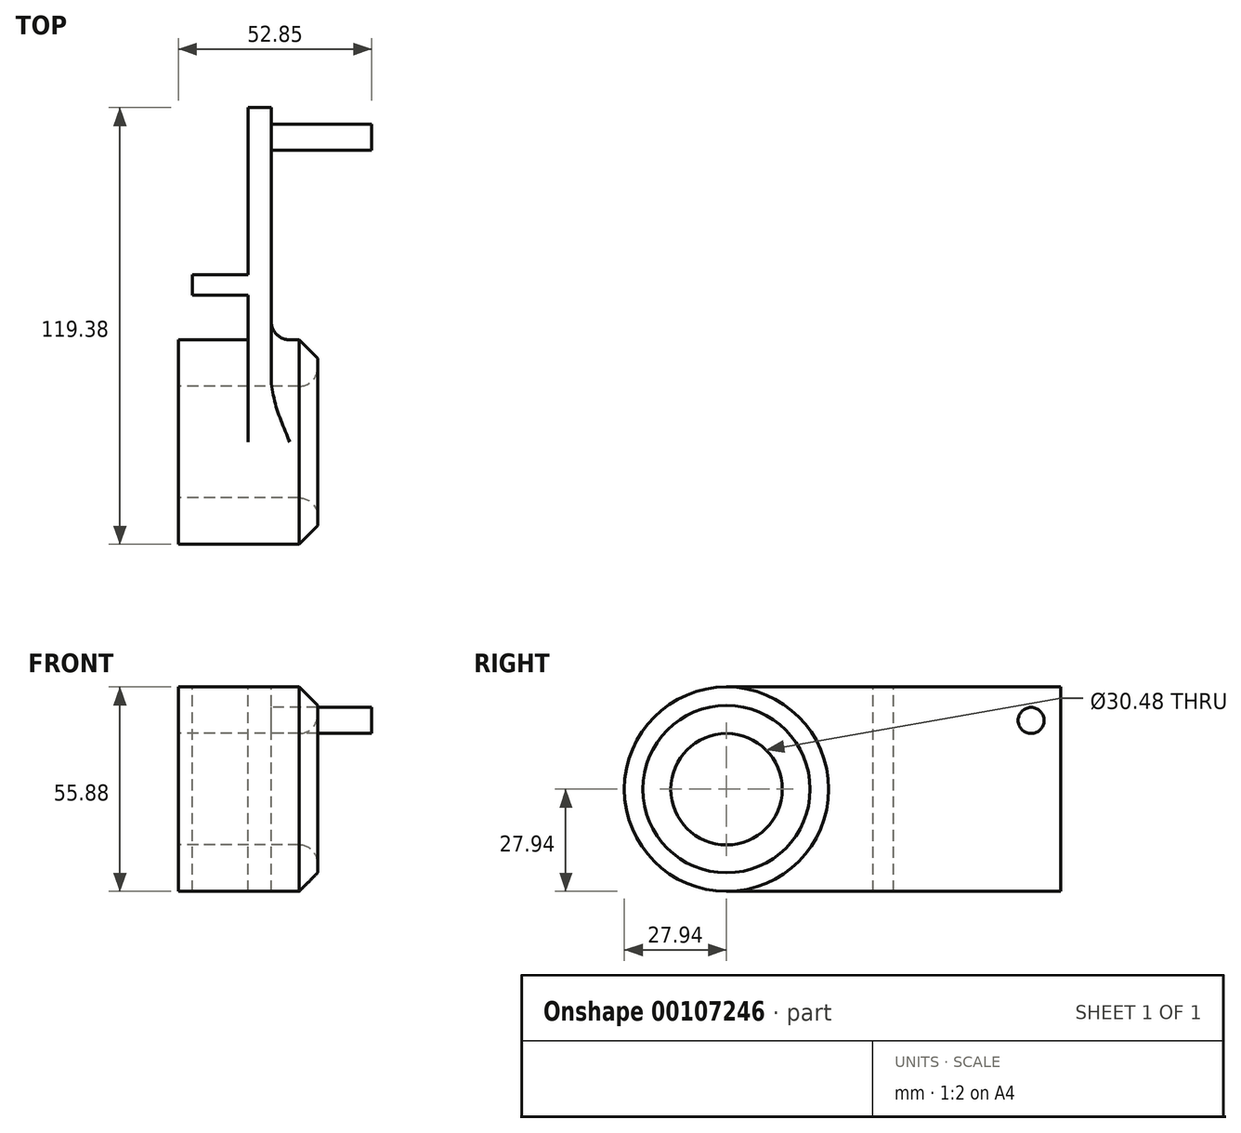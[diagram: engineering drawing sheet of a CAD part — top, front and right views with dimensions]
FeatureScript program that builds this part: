
annotation { "Feature Type Name" : "Feature", "Feature Type Description" : "" }
export const myFeature = defineFeature(function(context is Context, id is Id, definition is map)
    precondition{}
    {
        {
            var Q0;
            Q0=qCreatedBy(makeId("Right.planeOp"),FACE);
            var sketch = newSketch(context, id + "F0", { "sketchPlane" : qUnion([Q0])});
            skLineSegment(sketch, "E0.bottom", {"start": v(45.72, -27.94) * mm, "end": v(-45.72, -27.94) * mm});
            skLineSegment(sketch, "E0.top", {"start": v(45.72, 27.94) * mm, "end": v(-45.72, 27.94) * mm});
            skLineSegment(sketch, "E0.left", {"start": v(45.72, -27.94) * mm, "end": v(45.72, 27.94) * mm});
            skLineSegment(sketch, "E0.right", {"start": v(-45.72, -27.94) * mm, "end": v(-45.72, 27.94) * mm});
            skPoint(sketch, "E0.middle", {"position": v(0, 0) * mm});
            skCircle(sketch, "E1", {"center": v(-45.72, 0) * mm, "radius": 27.94 * mm});
            skCircle(sketch, "E2", {"center": v(-45.72, 0) * mm, "radius": 15.24 * mm});
            skSolve(sketch);
        }
        {
            var Q0;
            {var subQ0=sQuery(id+"F0.wireOp",EDGE,"E0.bottom");Q0=makeQuery(id+"F0.imprint","IMPRINT",FACE,{"disambiguationData":[TD([[makeQuery(id+"F0.imprint","IMPRINT",EDGE,{"derivedFrom":subQ0}),-1.0]])]});}
            var Q1;
            {var subQ1=sQuery(id+"F0.wireOp",EDGE,"E0.right");var subQ3=sQuery(id+"F0.wireOp",EDGE,"E2");var subQ4=makeQuery(id+"F0.imprint","INTERSECT",VERTEX,{"disambiguationData":[OD(0.0)],"derivedFrom":[subQ1,subQ3]});Q1=makeQuery(id+"F0.imprint","IMPRINT",FACE,{"disambiguationData":[TD([[makeQuery(id+"F0.imprint","IMPRINT",EDGE,{"disambiguationData":[TD([[subQ4,-1.0]])],"derivedFrom":subQ3}),-1.0]])]});}
            var Q2;
            {var subQ1=sQuery(id+"F0.wireOp",EDGE,"E0.right");var subQ3=sQuery(id+"F0.wireOp",EDGE,"E2");var subQ4=makeQuery(id+"F0.imprint","INTERSECT",VERTEX,{"disambiguationData":[OD(0.0)],"derivedFrom":[subQ1,subQ3]});Q2=makeQuery(id+"F0.imprint","IMPRINT",FACE,{"disambiguationData":[TD([[makeQuery(id+"F0.imprint","IMPRINT",EDGE,{"disambiguationData":[TD([[subQ4,1.0]])],"derivedFrom":subQ3}),-1.0]])]});}
            var Q3;
            {var subQ0=sQuery(id+"F0.wireOp",EDGE,"E2");var subQ1=sQuery(id+"F0.wireOp",EDGE,"E0.right");var subQ2=makeQuery(id+"F0.imprint","INTERSECT",VERTEX,{"disambiguationData":[OD(0.0)],"derivedFrom":[subQ1,subQ0]});Q3=makeQuery(id+"F0.imprint","IMPRINT",FACE,{"disambiguationData":[TD([[makeQuery(id+"F0.imprint","IMPRINT",EDGE,{"disambiguationData":[TD([[subQ2,-1.0]])],"derivedFrom":subQ1}),1.0]])]});}
            var Q4;
            {var subQ0=sQuery(id+"F0.wireOp",EDGE,"E2");var subQ1=sQuery(id+"F0.wireOp",EDGE,"E0.right");var subQ2=makeQuery(id+"F0.imprint","INTERSECT",VERTEX,{"disambiguationData":[OD(0.0)],"derivedFrom":[subQ1,subQ0]});Q4=makeQuery(id+"F0.imprint","IMPRINT",FACE,{"disambiguationData":[TD([[makeQuery(id+"F0.imprint","IMPRINT",EDGE,{"disambiguationData":[TD([[subQ2,-1.0]])],"derivedFrom":subQ1}),-1.0]])]});}
            extrude(context, id + "F1", {"entities" : qUnion([Q0, Q1, Q2, Q3, Q4]), "depth" : 6.35 * mm});
        }
        {
            var Q0;
            {var subQ1=sQuery(id+"F0.wireOp",EDGE,"E0.right");var subQ3=sQuery(id+"F0.wireOp",EDGE,"E2");var subQ4=makeQuery(id+"F0.imprint","INTERSECT",VERTEX,{"disambiguationData":[OD(0.0)],"derivedFrom":[subQ1,subQ3]});Q0=makeQuery(id+"F0.imprint","IMPRINT",FACE,{"disambiguationData":[TD([[makeQuery(id+"F0.imprint","IMPRINT",EDGE,{"disambiguationData":[TD([[subQ4,1.0]])],"derivedFrom":subQ3}),-1.0]])]});}
            var Q1;
            {var subQ1=sQuery(id+"F0.wireOp",EDGE,"E0.right");var subQ3=sQuery(id+"F0.wireOp",EDGE,"E2");var subQ4=makeQuery(id+"F0.imprint","INTERSECT",VERTEX,{"disambiguationData":[OD(0.0)],"derivedFrom":[subQ1,subQ3]});Q1=makeQuery(id+"F0.imprint","IMPRINT",FACE,{"disambiguationData":[TD([[makeQuery(id+"F0.imprint","IMPRINT",EDGE,{"disambiguationData":[TD([[subQ4,-1.0]])],"derivedFrom":subQ3}),-1.0]])]});}
            extrude(context, id + "F2", {"entities" : qUnion([Q0, Q1]), "operationType" : NewBodyOperationType.ADD, "endBound" : BoundingType.SYMMETRIC, "depth" : 38.1 * mm});
        }
        {
            var Q0;
            {var subQ0=sQuery(id+"F0.wireOp",EDGE,"E1");var subQ1=sQuery(id+"F0.wireOp",EDGE,"E0.left");var subQ2=sQuery(id+"F0.wireOp",EDGE,"E0.top");var subQ3=sQuery(id+"F0.wireOp",EDGE,"E0.bottom");Q0=makeQuery(id+"F2.boolean.opBoolean","SPLIT",FACE,{"disambiguationData":[TD([makeQuery(id+"F1.opExtrude","SWEPT_FACE",FACE,{"disambiguationData":[OSD([subQ3])]})])],"derivedFrom":makeQuery(id+"F1.opExtrude","CAP_FACE",FACE,{"disambiguationData":[OSD([subQ3,subQ2,subQ1,subQ0])],"isStart":false})});}
            var sketch = newSketch(context, id + "F3", { "sketchPlane" : qUnion([Q0])});
            skCircle(sketch, "E3", {"center": v(37.6, 18.8) * mm, "radius": 3.56 * mm});
            skSolve(sketch);
        }
        {
            var Q0;
            Q0=makeQuery(id+"F3.imprint","IMPRINT",FACE,{"disambiguationData":[TD([[makeQuery(id+"F3.imprint","IMPRINT",EDGE,{"derivedFrom":sQuery(id+"F3.wireOp",EDGE,"E3")}),1.0]])]});
            extrude(context, id + "F4", {"entities" : qUnion([Q0]), "operationType" : NewBodyOperationType.ADD, "depth" : 27.45 * mm});
        }
        {
            var Q0;
            Q0=makeQuery(id+"F2.opExtrude","CAP_EDGE",EDGE,{"disambiguationData":[OSD([sQuery(id+"F0.wireOp",EDGE,"E1")])],"isStart":false});
            chamfer(context, id + "F5", {"entities" : qUnion([Q0]), "width" : 5.08 * mm, "tangentPropagation" : true});
        }
        {
            var Q0;
            {var subQ0=sQuery(id+"F0.wireOp",EDGE,"E1");Q0=makeQuery(id+"F2.boolean.opBoolean","INTERSECT",EDGE,{"derivedFrom":[makeQuery(id+"F1.opExtrude","CAP_FACE",FACE,{"disambiguationData":[OSD([sQuery(id+"F0.wireOp",EDGE,"E0.bottom"),sQuery(id+"F0.wireOp",EDGE,"E0.top"),sQuery(id+"F0.wireOp",EDGE,"E0.left"),subQ0])],"isStart":false}),makeQuery(id+"F2.opExtrude","SWEPT_FACE",FACE,{"disambiguationData":[OSD([subQ0])]})]});}
            var Q1;
            Q1=makeQuery(id+"F2.opExtrude","CAP_EDGE",EDGE,{"disambiguationData":[OSD([sQuery(id+"F0.wireOp",EDGE,"E2")])],"isStart":false});
            fillet(context, id + "F6", {"entities" : qUnion([Q0, Q1]), "radius" : 5.08 * mm, "tangentPropagation" : true, "allowEdgeOverflow" : false});
        }
        {
            var Q0;
            {var subQ0=sQuery(id+"F0.wireOp",EDGE,"E0.bottom");Q0=makeQuery(id+"F0.imprint","IMPRINT",FACE,{"disambiguationData":[TD([[makeQuery(id+"F0.imprint","IMPRINT",EDGE,{"derivedFrom":subQ0}),-1.0]])]});}
            var sketch = newSketch(context, id + "F7", { "sketchPlane" : qUnion([Q0])});
            skLineSegment(sketch, "E4.bottom", {"start": v(-5.59, -27.94) * mm, "end": v(0, -27.94) * mm});
            skLineSegment(sketch, "E4.top", {"start": v(-5.59, 27.94) * mm, "end": v(0, 27.94) * mm});
            skLineSegment(sketch, "E4.left", {"start": v(-5.59, -27.94) * mm, "end": v(-5.59, 27.94) * mm});
            skLineSegment(sketch, "E4.right", {"start": v(0, -27.94) * mm, "end": v(0, 27.94) * mm});
            skSolve(sketch);
        }
        {
            var Q0;
            Q0 = qSketchRegion(id + "F7", true);
            extrude(context, id + "F8", {"entities" : qUnion([Q0]), "operationType" : NewBodyOperationType.ADD, "oppositeDirection" : true, "depth" : 15.24 * mm});
        }
        {
            var Q0;
            Q0=makeQuery(id+"F8.opExtrude","SWEPT_FACE",FACE,{"disambiguationData":[OSD([sQuery(id+"F7.wireOp",EDGE,"E4.right")])]});
            var sketch = newSketch(context, id + "F9", { "sketchPlane" : qUnion([Q0])});
            skSolve(sketch);
        }
    });
